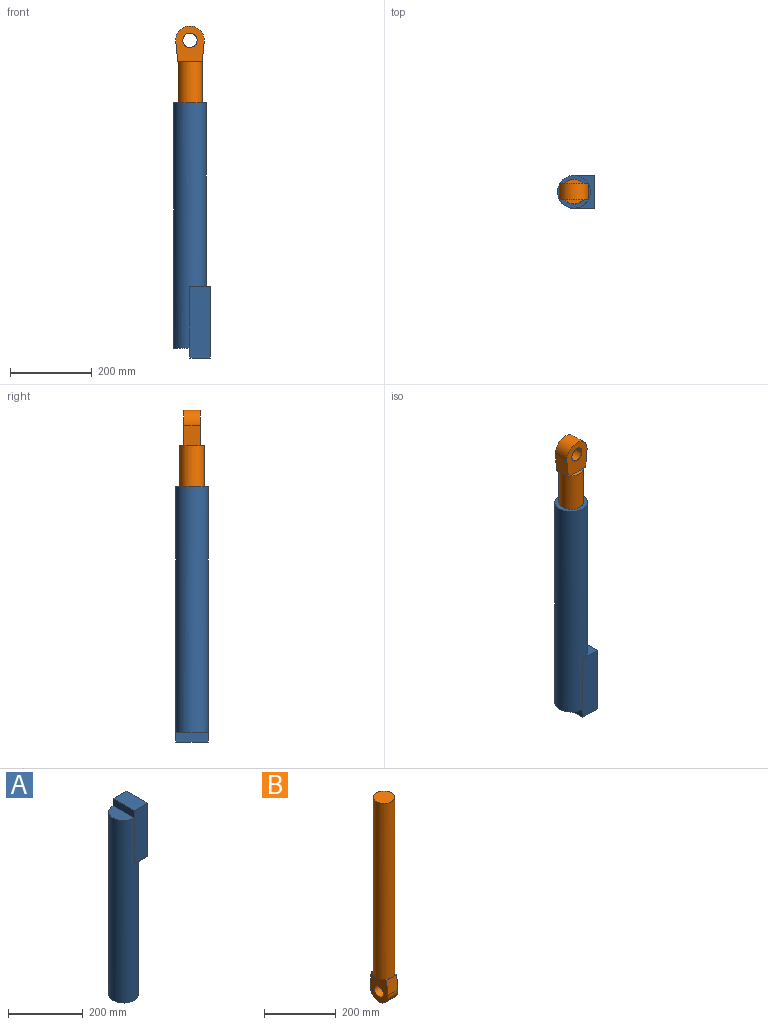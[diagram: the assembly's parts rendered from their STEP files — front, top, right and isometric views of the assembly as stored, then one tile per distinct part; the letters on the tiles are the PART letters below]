
ASSEMBLY  parts=2 mates=1
PART A: 11 faces, bbox 90x80x623.7 mm
  f0: cylinder r=40mm len=600mm, axis (0,0,-1), area 131777.4mm2, adj f1,f2,f4,f7,f8
  f1: plane 80x40mm, normal (0,0,1), area 2513.3mm2, adj f0,f3
  f2: plane 80x80mm, normal (0,0,-1), area 2199.1mm2, adj f0,f9
  f3: plane 80x23.65mm, normal (-1,0,0), area 1892.1mm2, adj f1,f6,f7,f8
  f4: plane 80x50mm, normal (0,0,-1), area 1486.7mm2, adj f0,f5,f7,f8
  f5: plane 175x80mm, normal (1,0,0), area 14000mm2, adj f4,f6,f7,f8
  f6: plane 80x50mm, normal (0,0,1), area 4000mm2, adj f3,f5,f7,f8
  f7: plane 175x50mm, normal (0,-1,0), area 8750mm2, adj f0,f3,f4,f5,f6
  f8: plane 175x50mm, normal (0,1,0), area 8750mm2, adj f0,f3,f4,f5,f6
  f9: cylinder r=30mm len=500mm, axis (0,0,-1), area 94247.8mm2, adj f2,f10
  f10: plane 60x60mm, normal (0,0,-1), area 2827.4mm2, adj f9
PART B: 14 faces, bbox 60x70x687.6 mm
  f0: plane 6.45x0.17mm, normal (0,0,-1), area 0.7mm2, adj f2,f9
  f1: plane 44.72x10mm, normal (0,0,-1), area 309.7mm2, adj f2,f11
  f2: cylinder r=30mm len=600mm, axis (0,0,-1), area 113097.3mm2, adj f0,f1,f3,f4,f5,f6,f8
  f3: plane 60x60mm, normal (0,0,1), area 2827.4mm2, adj f2
  f4: plane 44.72x10mm, normal (0,0,-1), area 309.7mm2, adj f2,f12
  f5: plane 40x7.81mm, normal (0,0,1), area 103mm2, adj f2,f7,f11,f12
  f6: plane 16.78x7.47mm, normal (0,0,1), area 44.9mm2, adj f2,f9,f12
  f7: plane 49.29x40mm, normal (0,1,0.09), area 1980.3mm2, adj f5,f10,f11,f12
  f8: plane 16.78x7.47mm, normal (0,0,1), area 44.9mm2, adj f2,f9,f11
  f9: plane 49.04x40mm, normal (0,-0.99,0.1), area 1971.9mm2, adj f0,f6,f8,f10,f11,f12
  f10: cylinder r=35mm len=70mm, axis (-1,0,0), area 4672.5mm2, adj f7,f9,f11,f12
  f11: plane 87.59x70mm, normal (1,0,0), area 4388.9mm2, adj f1,f5,f7,f8,f9,f10,f13
  f12: plane 87.59x70mm, normal (-1,0,0), area 4388.9mm2, adj f4,f5,f6,f7,f9,f10,f13
  f13: cylinder r=17.5mm len=40mm, axis (-1,0,0), area 4398.2mm2, adj f11,f12
PLACE A rot(axis=(1,0,0),180deg) t=(-193.87,-31.79,305.87)mm
PLACE B rot(axis=(0.71,0.71,0),180deg) t=(-193.87,-31.79,405.87)mm
MATE slider B.f2 <-> A.f0  axis (0,0,1) through (-193.87,-31.79,-194.13)mm
